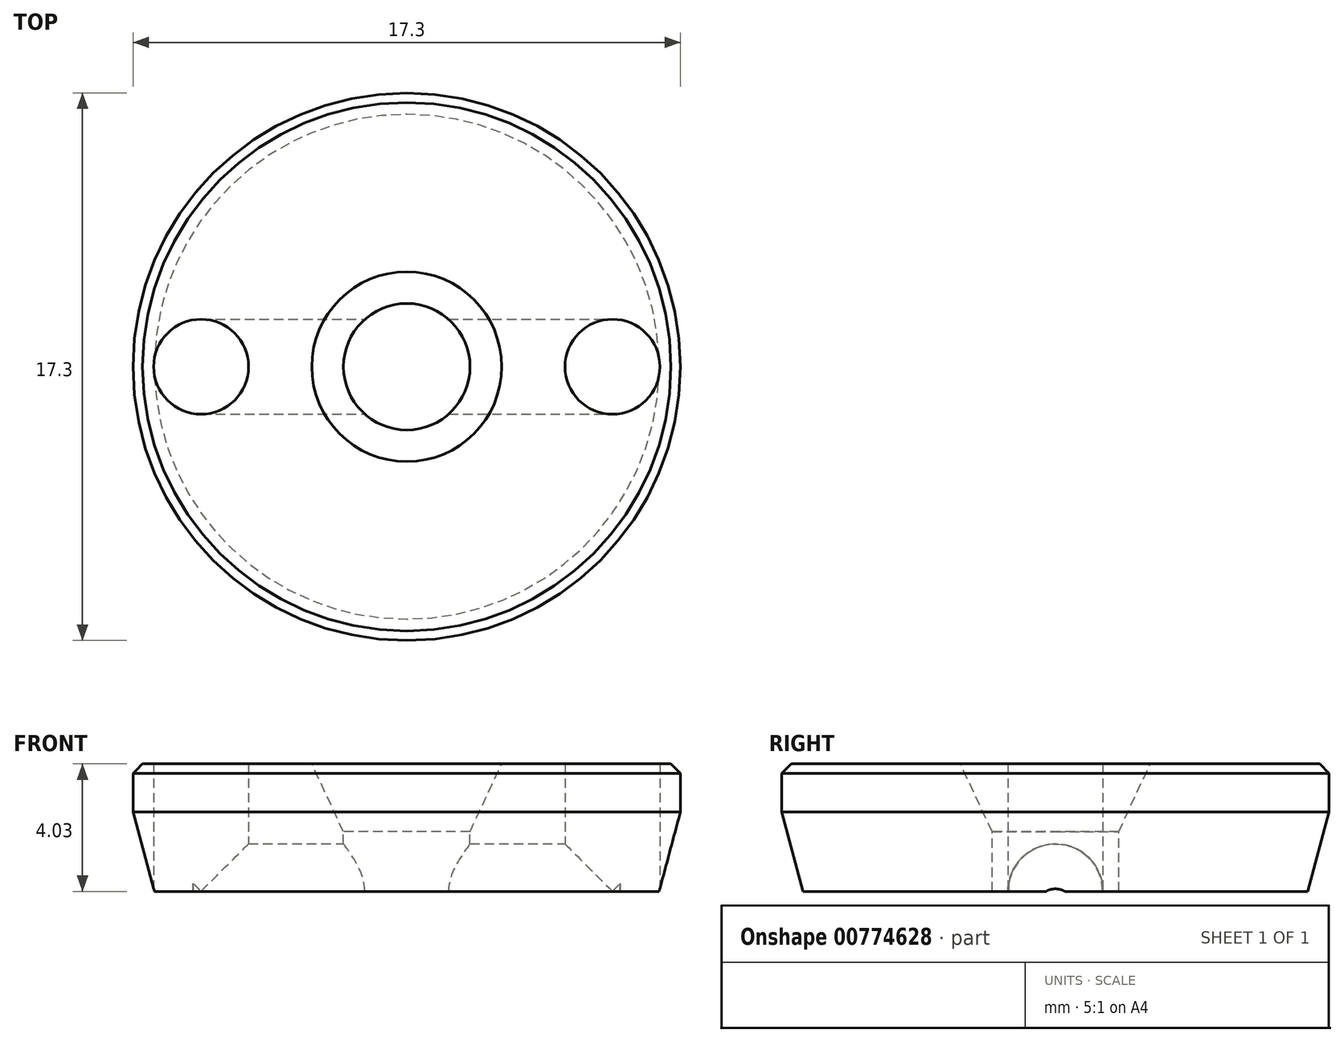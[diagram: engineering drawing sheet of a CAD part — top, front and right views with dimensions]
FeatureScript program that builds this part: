
annotation { "Feature Type Name" : "Feature", "Feature Type Description" : "" }
export const myFeature = defineFeature(function(context is Context, id is Id, definition is map)
    precondition{}
    {
        {
            var Q0;
            Q0=qCreatedBy(makeId("Front.planeOp"),FACE);
            var sketch = newSketch(context, id + "F0", { "sketchPlane" : qUnion([Q0])});
            skLineSegment(sketch, "E0", {"start": v(-7.65, 53) * mm, "end": v(-3, 53) * mm});
            skLineSegment(sketch, "E1", {"start": v(-3, 53) * mm, "end": v(-2, 50.86) * mm});
            skLineSegment(sketch, "E2", {"start": v(-2, 50.86) * mm, "end": v(-2, 48.97) * mm});
            skPoint(sketch, "E3.orphan", {"position": v(0, 53) * mm});
            skLineSegment(sketch, "E4", {"start": v(-8, 0) * mm, "end": v(-8, 0) * mm});
            skPoint(sketch, "E5.end.orphan", {"position": v(0, 66) * mm});
            skPoint(sketch, "E6.visualSharp", {"position": v(-10, 0) * mm});
            skPoint(sketch, "E7.visualSharp", {"position": v(-8, 0) * mm});
            skPoint(sketch, "E8.visualSharp", {"position": v(-17.5, -11) * mm});
            skLineSegment(sketch, "E9", {"start": v(0, 75.07) * mm, "end": v(0, -45.35) * mm});
            skPoint(sketch, "E10.visualSharp", {"position": v(-8.65, 53) * mm});
            skLineSegment(sketch, "E11", {"start": v(-8.65, 53) * mm, "end": v(-8.65, 51.48) * mm});
            skLineSegment(sketch, "E12", {"start": v(-7.98, 48.97) * mm, "end": v(-2, 48.97) * mm});
            skLineSegment(sketch, "E13", {"start": v(0, 48.97) * mm, "end": v(0, 49.56) * mm});
            skLineSegment(sketch, "E14", {"start": v(-7.65, 53) * mm, "end": v(-8.65, 53) * mm});
            skLineSegment(sketch, "E15", {"start": v(-8.65, 51.48) * mm, "end": v(-7.98, 48.97) * mm});
            skPoint(sketch, "E16.orphan", {"position": v(-8.65, 48.97) * mm});
            skPoint(sketch, "E17.start.orphan", {"position": v(-8.65, 54) * mm});
            skPoint(sketch, "E18.start.orphan", {"position": v(-17.5, 66) * mm});
            skPoint(sketch, "E19.end.orphan", {"position": v(-10, -20) * mm});
            skPoint(sketch, "E20.start.orphan", {"position": v(-24.75, -11) * mm});
            skSolve(sketch);
        }
        {
            var Q0;
            Q0=makeQuery(id+"F0.imprint","IMPRINT",FACE,{"disambiguationData":[TD([[makeQuery(id+"F0.imprint","IMPRINT",EDGE,{"derivedFrom":sQuery(id+"F0.wireOp",EDGE,"E0")}),-1.0]])]});
            var Q1;
            Q1=sQuery(id+"F0.wireOp",EDGE,"E9");
            revolve(context, id + "F1", {"surfaceOperationType" : NewSurfaceOperationType.NEW, "entities" : qUnion([Q0]), "axis" : qUnion([Q1]), "revolveType" : RevolveType.FULL});
        }
        {
            var Q0;
            Q0=makeQuery(id+"F1.opRevolve","SWEPT_EDGE",EDGE,{"disambiguationData":[OSD([sQuery(id+"F0.wireOp",EDGE,"E11"),sQuery(id+"F0.wireOp",EDGE,"E14")])]});
            chamfer(context, id + "F2", {"entities" : qUnion([Q0]), "width" : 0.3 * mm, "tangentPropagation" : true});
        }
        {
            var Q0;
            Q0=qCreatedBy(makeId("Top.planeOp"),FACE);
            var sketch = newSketch(context, id + "F3", { "sketchPlane" : qUnion([Q0])});
            skLineSegment(sketch, "E21", {"start": v(0, 0) * mm, "end": v(6.5, 0) * mm});
            skLineSegment(sketch, "E22", {"start": v(0, 0) * mm, "end": v(-6.5, 0) * mm});
            skCircle(sketch, "E23", {"center": v(-6.5, 0) * mm, "radius": 1.5 * mm});
            skCircle(sketch, "E24", {"center": v(6.5, 0) * mm, "radius": 1.5 * mm});
            skSolve(sketch);
        }
        {
            var Q0;
            Q0=makeQuery(id+"F3.imprint","IMPRINT",FACE,{"disambiguationData":[TD([[makeQuery(id+"F3.imprint","IMPRINT",EDGE,{"derivedFrom":sQuery(id+"F3.wireOp",EDGE,"E23")}),1.0]])]});
            var Q1;
            Q1=makeQuery(id+"F3.imprint","IMPRINT",FACE,{"disambiguationData":[TD([[makeQuery(id+"F3.imprint","IMPRINT",EDGE,{"derivedFrom":sQuery(id+"F3.wireOp",EDGE,"E24")}),1.0]])]});
            extrude(context, id + "F4", {"entities" : qUnion([Q0, Q1]), "operationType" : NewBodyOperationType.REMOVE, "depth" : 80 * mm, "offsetDistance" : 25 * mm});
        }
        {
            var Q0;
            Q0=qCreatedBy(makeId("Right.planeOp"),FACE);
            var sketch = newSketch(context, id + "F5", { "sketchPlane" : qUnion([Q0])});
            skCircle(sketch, "E25", {"center": v(0, 48.97) * mm, "radius": 1.5 * mm});
            skSolve(sketch);
        }
        {
            var Q0;
            Q0=makeQuery(id+"F5.imprint","IMPRINT",FACE,{"disambiguationData":[TD([[makeQuery(id+"F5.imprint","IMPRINT",EDGE,{"derivedFrom":sQuery(id+"F5.wireOp",EDGE,"E25")}),1.0]])]});
            extrude(context, id + "F6", {"entities" : qUnion([Q0]), "operationType" : NewBodyOperationType.REMOVE, "endBound" : BoundingType.SYMMETRIC, "oppositeDirection" : true, "depth" : 13.5 * mm, "offsetDistance" : 25 * mm});
        }
    });
